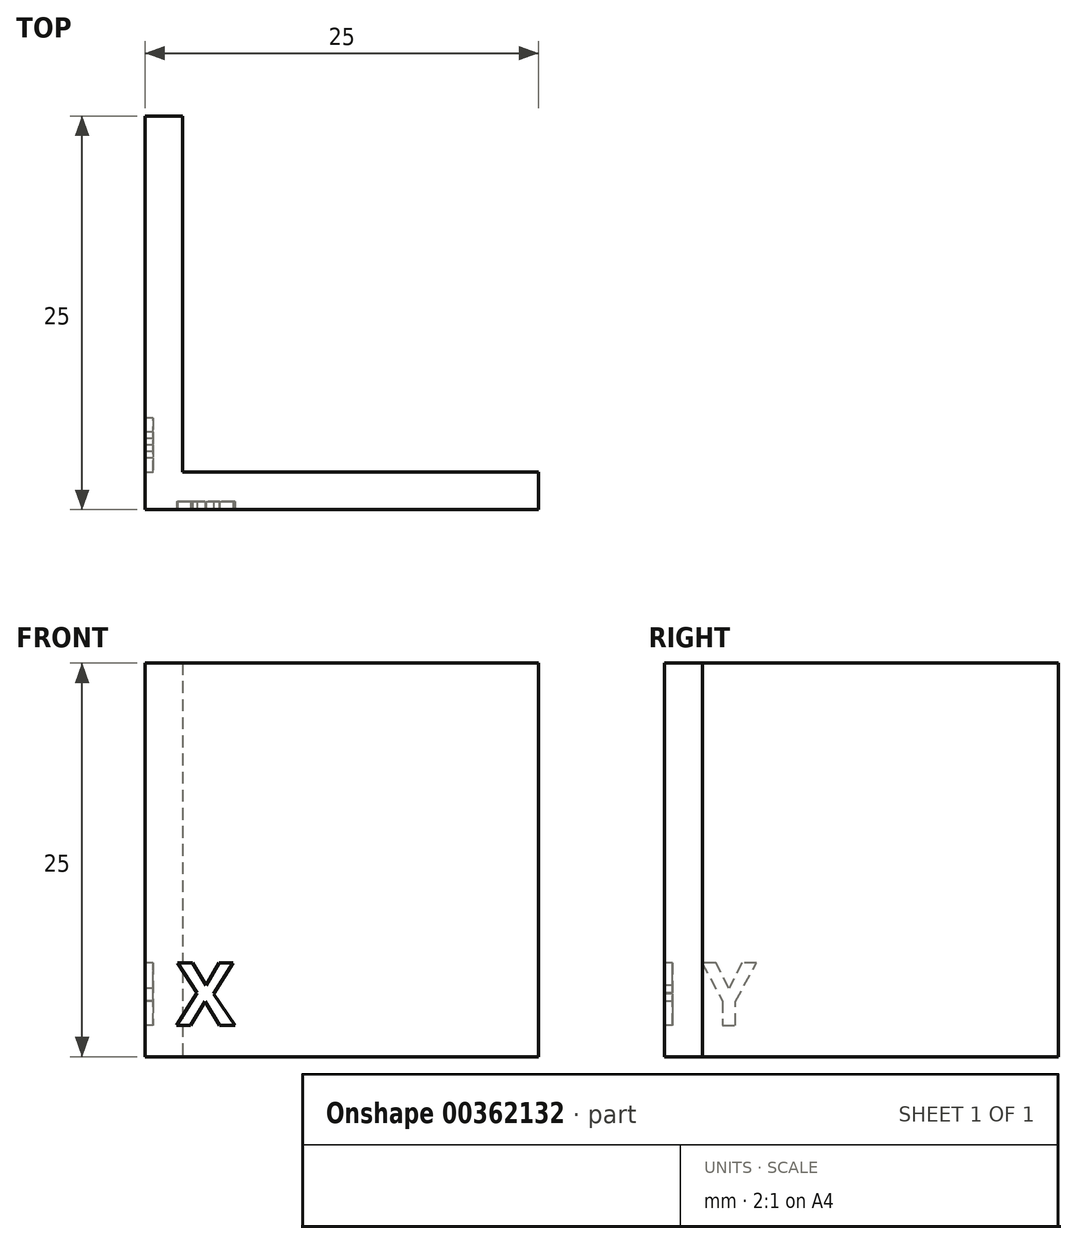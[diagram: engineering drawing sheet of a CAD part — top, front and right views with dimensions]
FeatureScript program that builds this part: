
annotation { "Feature Type Name" : "Feature", "Feature Type Description" : "" }
export const myFeature = defineFeature(function(context is Context, id is Id, definition is map)
    precondition{}
    {
        {
            var Q0;
            Q0=qCreatedBy(makeId("Top.planeOp"),FACE);
            var sketch = newSketch(context, id + "F0", { "sketchPlane" : qUnion([Q0])});
            skLineSegment(sketch, "E0.bottom", {"start": v(0, 0) * mm, "end": v(25, 0) * mm});
            skLineSegment(sketch, "E0.top", {"start": v(0, 25) * mm, "end": v(25, 25) * mm});
            skLineSegment(sketch, "E0.left", {"start": v(0, 0) * mm, "end": v(0, 25) * mm});
            skLineSegment(sketch, "E0.right", {"start": v(25, 0) * mm, "end": v(25, 25) * mm});
            skLineSegment(sketch, "E1.bottom", {"start": v(25, 25) * mm, "end": v(2.4, 25) * mm});
            skLineSegment(sketch, "E1.top", {"start": v(25, 2.4) * mm, "end": v(2.4, 2.4) * mm});
            skLineSegment(sketch, "E1.left", {"start": v(25, 25) * mm, "end": v(25, 2.4) * mm});
            skLineSegment(sketch, "E1.right", {"start": v(2.4, 25) * mm, "end": v(2.4, 2.4) * mm});
            skSolve(sketch);
        }
        {
            var Q0;
            Q0=makeQuery(id+"F0.imprint","IMPRINT",FACE,{"disambiguationData":[TD([[makeQuery(id+"F0.imprint","IMPRINT",EDGE,{"derivedFrom":sQuery(id+"F0.wireOp",EDGE,"E0.bottom")}),1.0]])]});
            extrude(context, id + "F1", {"entities" : qUnion([Q0]), "depth" : 25 * mm, "offsetDistance" : 25 * mm});
        }
        {
            var Q0;
            Q0=makeQuery(id+"F1.opExtrude","SWEPT_FACE",FACE,{"disambiguationData":[OSD([sQuery(id+"F0.wireOp",EDGE,"E0.bottom")])]});
            var sketch = newSketch(context, id + "F2", { "sketchPlane" : qUnion([Q0])});
            skText(sketch, "E2", { "text": "X", "fontName": "OpenSans-Bold.ttf"});
            const initialGuessF2  = {"E2": [0.002, 0.002, 1, 0, 0.004]};
            skSetInitialGuess(sketch, initialGuessF2);
            skSolve(sketch);
        }
        {
            var Q0;
            Q0=makeQuery(id+"F2.imprint","IMPRINT",FACE,{"disambiguationData":[TD([[makeQuery(id+"F2.imprint","IMPRINT",EDGE,{"derivedFrom":sQuery(id+"F2.wireOp",EDGE,"E2.sketch_text.stroke-0")}),-1.0]])]});
            extrude(context, id + "F3", {"entities" : qUnion([Q0]), "operationType" : NewBodyOperationType.REMOVE, "oppositeDirection" : true, "depth" : 0.5 * mm, "offsetDistance" : 25 * mm});
        }
        {
            var Q0;
            Q0=makeQuery(id+"F1.opExtrude","SWEPT_FACE",FACE,{"disambiguationData":[OSD([sQuery(id+"F0.wireOp",EDGE,"E0.left")])]});
            var sketch = newSketch(context, id + "F4", { "sketchPlane" : qUnion([Q0])});
            skText(sketch, "E3", { "text": "Y", "fontName": "OpenSans-Bold.ttf"});
            const initialGuessF4  = {"E3": [-0.00583, 0.002, 1, 0, 0.004]};
            skSetInitialGuess(sketch, initialGuessF4);
            skSolve(sketch);
        }
        {
            var Q0;
            Q0=makeQuery(id+"F4.imprint","IMPRINT",FACE,{"disambiguationData":[TD([[makeQuery(id+"F4.imprint","IMPRINT",EDGE,{"derivedFrom":sQuery(id+"F4.wireOp",EDGE,"E3.sketch_text.stroke-0")}),-1.0]])]});
            extrude(context, id + "F5", {"entities" : qUnion([Q0]), "operationType" : NewBodyOperationType.REMOVE, "oppositeDirection" : true, "depth" : 0.5 * mm, "offsetDistance" : 25 * mm});
        }
    });
